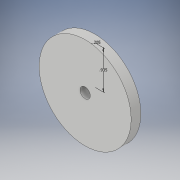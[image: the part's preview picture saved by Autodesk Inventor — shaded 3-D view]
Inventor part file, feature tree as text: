
AUTODESK INVENTOR PART (.ipt)
format: ipt  version: 2017 (Build 210142000, 142)  size: 100,352 bytes
history: native  units: in
note: dims shown in document units (in); Inventor stores cm internally (conversion verified against a paired STEP export)
features: sketch x3, extrude x1, hole x1
ambient origin geometry x8: Origin, YZ Plane, XZ Plane, XY Plane, X Axis, Y Axis, Z Axis, Center Point
bodies: Solid1 (feature_tree)
feature tree (5):
  extrude  "Extrusion1"  Depth=0.236in TaperAngle=0.0deg
  hole  "Hole1"  [1 undecoded]
  sketch  "Sketch3"  dims[d11=0.205in]
  sketch  "Sketch1"  dims[d0=2.236in d1=0.236in d2=0.0in]
  sketch  "Sketch2"  dims[d3=0.25in d4=0.75in d5=0.375in d6=0.25in d7=0.5635in d8=0.236in d9=0.0in d10=0.935in]
note: 1 required parameter value undecoded (feature->parameter linkage not recoverable at this tier; creation-order binding heuristic only, values carry confidence <= 0.55)
